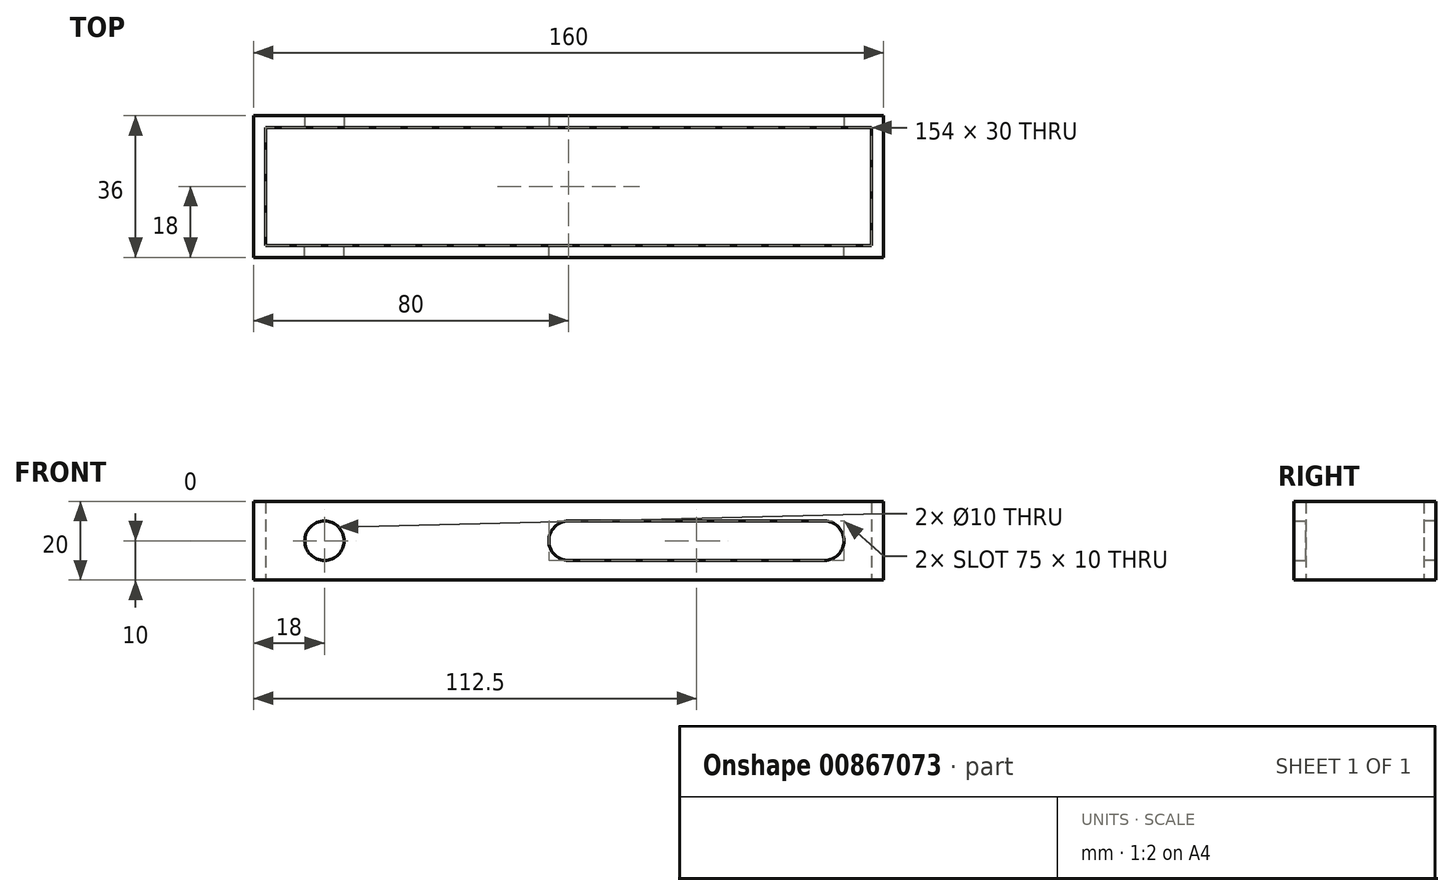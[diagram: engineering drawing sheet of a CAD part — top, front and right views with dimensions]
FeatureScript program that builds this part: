
annotation { "Feature Type Name" : "Feature", "Feature Type Description" : "" }
export const myFeature = defineFeature(function(context is Context, id is Id, definition is map)
    precondition{}
    {
        {
            var Q0;
            Q0=qCreatedBy(makeId("Front.planeOp"),FACE);
            cPlane(context, id + "F0", {"entities" : qUnion([Q0]), "cplaneType" : CPlaneType.OFFSET, "offset" : 15 * mm, "width" : 150 * mm, "height" : 150 * mm});
        }
        {
            var Q0;
            Q0=qCreatedBy(id+"F0.planeOp",FACE);
            var sketch = newSketch(context, id + "F1", { "sketchPlane" : qUnion([Q0])});
            skLineSegment(sketch, "E0.bottom", {"start": v(-80, 0) * mm, "end": v(80, 0) * mm});
            skLineSegment(sketch, "E0.top", {"start": v(-80, 20) * mm, "end": v(80, 20) * mm});
            skLineSegment(sketch, "E0.left", {"start": v(-80, 0) * mm, "end": v(-80, 20) * mm});
            skLineSegment(sketch, "E0.right", {"start": v(80, 0) * mm, "end": v(80, 20) * mm});
            skLineSegment(sketch, "E1", {"start": v(-77, 20) * mm, "end": v(-77, 0) * mm});
            skLineSegment(sketch, "E2", {"start": v(-67, 20) * mm, "end": v(-67, 0) * mm});
            skLineSegment(sketch, "E3", {"start": v(77, 20) * mm, "end": v(77, 0) * mm});
            skLineSegment(sketch, "E4", {"start": v(-80, 0) * mm, "end": v(-77, 0) * mm});
            skLineSegment(sketch, "E5", {"start": v(-67, 0) * mm, "end": v(67, 0) * mm});
            skLineSegment(sketch, "E6", {"start": v(77, 0) * mm, "end": v(80, 0) * mm});
            skLineSegment(sketch, "E7", {"start": v(-77, 0) * mm, "end": v(-67, 0) * mm});
            skLineSegment(sketch, "E8", {"start": v(67, 0) * mm, "end": v(77, 0) * mm});
            skLineSegment(sketch, "E9", {"start": v(80, 0) * mm, "end": v(77, 0) * mm});
            skCircle(sketch, "E10", {"center": v(-62, 10) * mm, "radius": 5 * mm});
            skPoint(sketch, "E11", {"position": v(-67, 10) * mm});
            skCircle(sketch, "E12", {"center": v(65, 10) * mm, "radius": 5 * mm});
            skPoint(sketch, "E12.centerSnap0", {"position": v(70, 10) * mm});
            skLineSegment(sketch, "E13", {"start": v(0, 20) * mm, "end": v(0, 0) * mm});
            skCircle(sketch, "E14", {"center": v(0, 10) * mm, "radius": 5 * mm});
            skLineSegment(sketch, "E15", {"start": v(0, 15) * mm, "end": v(65, 15) * mm});
            skLineSegment(sketch, "E16", {"start": v(65, 15) * mm, "end": v(65, 5) * mm});
            skLineSegment(sketch, "E17", {"start": v(65, 5) * mm, "end": v(0, 5) * mm});
            skLineSegment(sketch, "E18", {"start": v(-80, 10) * mm, "end": v(80, 10) * mm, "construction": true});
            skSolve(sketch);
        }
        {
            var Q0;
            {var subQ0=sQuery(id+"F1.wireOp",EDGE,"E0.right");Q0=makeQuery(id+"F1.imprint","IMPRINT",FACE,{"disambiguationData":[TD([[makeQuery(id+"F1.imprint","IMPRINT",EDGE,{"derivedFrom":subQ0}),1.0]])]});}
            var Q1;
            {var subQ0=sQuery(id+"F1.wireOp",EDGE,"E0.left");Q1=makeQuery(id+"F1.imprint","IMPRINT",FACE,{"disambiguationData":[TD([[makeQuery(id+"F1.imprint","IMPRINT",EDGE,{"derivedFrom":subQ0}),-1.0]])]});}
            var Q2;
            Q2=qCreatedBy(makeId("Front.planeOp"),FACE);
            extrude(context, id + "F2", {"entities" : qUnion([Q0, Q1]), "endBound" : BoundingType.UP_TO_SURFACE, "oppositeDirection" : true, "depth" : 25 * mm, "endBoundEntityFace" : qUnion([Q2]), "offsetDistance" : 25 * mm});
        }
        {
            var Q0;
            {var subQ0=sQuery(id+"F1.wireOp",EDGE,"E3");Q0=makeQuery(id+"F1.imprint","IMPRINT",FACE,{"disambiguationData":[TD([[makeQuery(id+"F1.imprint","IMPRINT",EDGE,{"derivedFrom":subQ0}),-1.0]])]});}
            var Q1;
            {var subQ3=sQuery(id+"F1.wireOp",EDGE,"E15");Q1=makeQuery(id+"F1.imprint","IMPRINT",FACE,{"disambiguationData":[TD([[makeQuery(id+"F1.imprint","IMPRINT",EDGE,{"derivedFrom":subQ3}),1.0]])]});}
            var Q2;
            {var subQ0=sQuery(id+"F1.wireOp",EDGE,"E17");Q2=makeQuery(id+"F1.imprint","IMPRINT",FACE,{"disambiguationData":[TD([[makeQuery(id+"F1.imprint","IMPRINT",EDGE,{"derivedFrom":subQ0}),1.0]])]});}
            var Q3;
            {var subQ7=sQuery(id+"F1.wireOp",EDGE,"E10");Q3=makeQuery(id+"F1.imprint","IMPRINT",FACE,{"disambiguationData":[TD([[makeQuery(id+"F1.imprint","IMPRINT",EDGE,{"derivedFrom":subQ7}),-1.0]])]});}
            var Q4;
            {var subQ5=sQuery(id+"F1.wireOp",EDGE,"E1");Q4=makeQuery(id+"F1.imprint","IMPRINT",FACE,{"disambiguationData":[TD([[makeQuery(id+"F1.imprint","IMPRINT",EDGE,{"derivedFrom":subQ5}),1.0]])]});}
            var Q5;
            {var subQ0=sQuery(id+"F1.wireOp",EDGE,"E0.left");Q5=makeQuery(id+"F1.imprint","IMPRINT",FACE,{"disambiguationData":[TD([[makeQuery(id+"F1.imprint","IMPRINT",EDGE,{"derivedFrom":subQ0}),-1.0]])]});}
            var Q6;
            {var subQ0=sQuery(id+"F1.wireOp",EDGE,"E0.right");Q6=makeQuery(id+"F1.imprint","IMPRINT",FACE,{"disambiguationData":[TD([[makeQuery(id+"F1.imprint","IMPRINT",EDGE,{"derivedFrom":subQ0}),1.0]])]});}
            extrude(context, id + "F3", {"entities" : qUnion([Q0, Q1, Q2, Q3, Q4, Q5, Q6]), "operationType" : NewBodyOperationType.ADD, "depth" : 3 * mm, "offsetDistance" : 25 * mm});
        }
        {
            var Q0;
            Q0=makeQuery(id+"F2.opExtrude","SWEPT_BODY",BODY,{"disambiguationData":[OSD([sQuery(id+"F1.wireOp",EDGE,"E0.top"),sQuery(id+"F1.wireOp",EDGE,"E0.right"),sQuery(id+"F1.wireOp",EDGE,"E3"),sQuery(id+"F1.wireOp",EDGE,"E9")])]});
            var Q1;
            Q1=makeQuery(id+"F3.opExtrude","SWEPT_BODY",BODY,{"disambiguationData":[OSD([sQuery(id+"F1.wireOp",EDGE,"E0.top"),sQuery(id+"F1.wireOp",EDGE,"E0.left"),sQuery(id+"F1.wireOp",EDGE,"E0.right"),sQuery(id+"F1.wireOp",EDGE,"E4"),sQuery(id+"F1.wireOp",EDGE,"E5"),sQuery(id+"F1.wireOp",EDGE,"E7"),sQuery(id+"F1.wireOp",EDGE,"E8"),sQuery(id+"F1.wireOp",EDGE,"E9"),sQuery(id+"F1.wireOp",EDGE,"E10"),sQuery(id+"F1.wireOp",EDGE,"E12"),sQuery(id+"F1.wireOp",EDGE,"E14"),sQuery(id+"F1.wireOp",EDGE,"E15"),sQuery(id+"F1.wireOp",EDGE,"E17")])]});
            var Q2;
            Q2=makeQuery(id+"F2.opExtrude","SWEPT_BODY",BODY,{"disambiguationData":[OSD([sQuery(id+"F1.wireOp",EDGE,"E0.top"),sQuery(id+"F1.wireOp",EDGE,"E0.left"),sQuery(id+"F1.wireOp",EDGE,"E1"),sQuery(id+"F1.wireOp",EDGE,"E4")])]});
            var Q3;
            Q3=qCreatedBy(makeId("Front.planeOp"),FACE);
            mirror(context, id + "F4", {"operationType" : NewBodyOperationType.ADD, "entities" : qUnion([Q0, Q1, Q2]), "mirrorPlane" : qUnion([Q3])});
        }
    });
